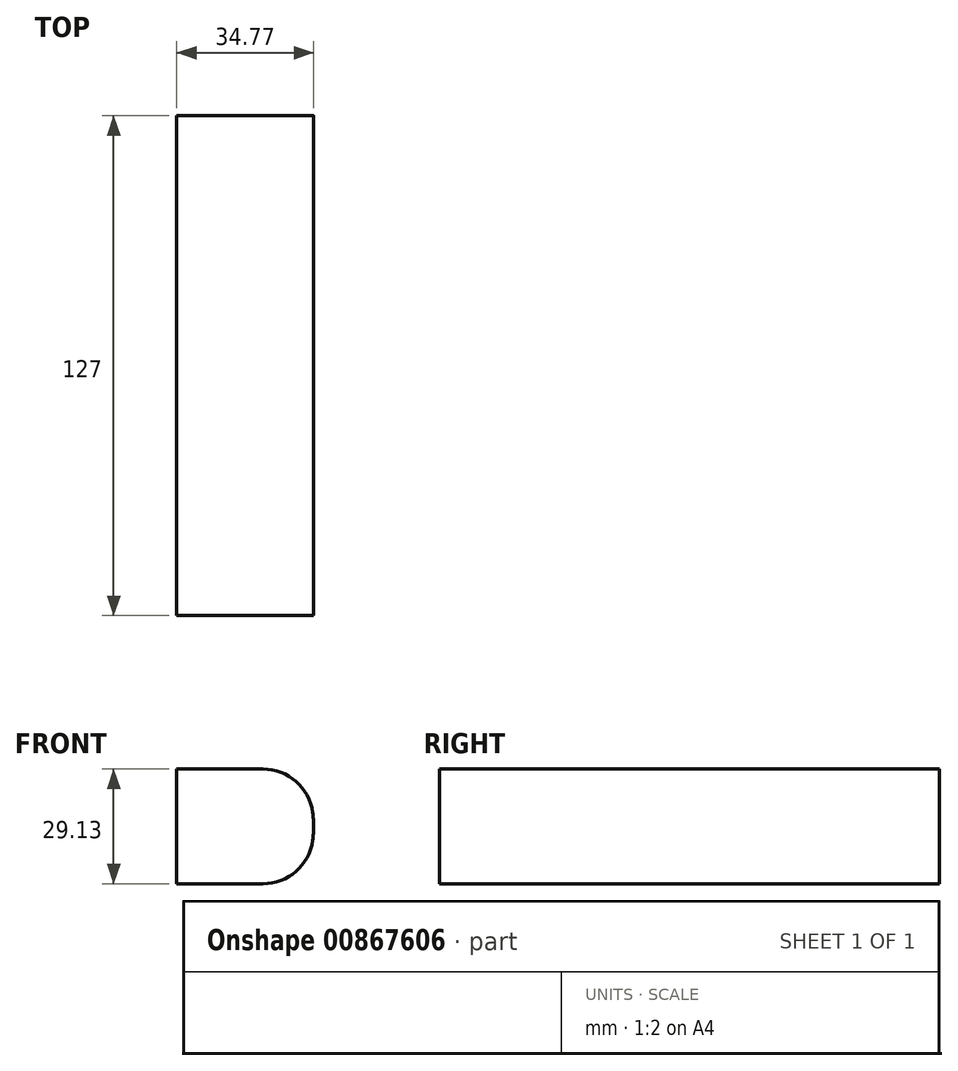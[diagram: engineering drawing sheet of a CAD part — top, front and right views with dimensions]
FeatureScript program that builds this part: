
annotation { "Feature Type Name" : "Feature", "Feature Type Description" : "" }
export const myFeature = defineFeature(function(context is Context, id is Id, definition is map)
    precondition{}
    {
        {
            var Q0;
            Q0=qCreatedBy(makeId("Front.planeOp"),FACE);
            var sketch = newSketch(context, id + "F0", { "sketchPlane" : qUnion([Q0])});
            skLineSegment(sketch, "E0.bottom", {"start": v(-28.16, 11.32) * mm, "end": v(2.25, 11.32) * mm});
            skLineSegment(sketch, "E0.top", {"start": v(-28.16, -17.81) * mm, "end": v(2.25, -17.81) * mm});
            skLineSegment(sketch, "E0.left", {"start": v(-28.16, 11.32) * mm, "end": v(-28.16, -17.81) * mm});
            skLineSegment(sketch, "E0.right", {"start": v(2.25, 11.32) * mm, "end": v(2.25, -17.81) * mm});
            skArc(sketch, "E1", {"start": v(2.25, -17.81) * mm, "mid": v(6.6, -3.25) * mm, "end": v(2.25, 11.32) * mm});
            skSolve(sketch);
        }
        {
            var Q0;
            Q0 = qSketchRegion(id + "F0", true);
            extrude(context, id + "F1", {"entities" : qUnion([Q0]), "depth" : 127 * mm, "offsetDistance" : 25.4 * mm});
        }
        {
            var Q0;
            Q0=makeQuery(id+"F1.opExtrude","SWEPT_EDGE",EDGE,{"disambiguationData":[OSD([sQuery(id+"F0.wireOp",EDGE,"E0.bottom"),sQuery(id+"F0.wireOp",EDGE,"E0.right"),sQuery(id+"F0.wireOp",EDGE,"E1")])]});
            var Q1;
            Q1=makeQuery(id+"F1.opExtrude","SWEPT_EDGE",EDGE,{"disambiguationData":[OSD([sQuery(id+"F0.wireOp",EDGE,"E0.top"),sQuery(id+"F0.wireOp",EDGE,"E0.right"),sQuery(id+"F0.wireOp",EDGE,"E1")])]});
            fillet(context, id + "F2", {"entities" : qUnion([Q0, Q1]), "radius" : 12.7 * mm, "tangentPropagation" : true, "allowEdgeOverflow" : false});
        }
    });
